# Revit family: equip-sink-elkay-double-lustertone-3322
name_source: partatom
category: Generic Models
units: mm (PartAtom-declared; Revit-internal decimal feet)

## family parameters
Always vertical = Yes
Can host rebar = No
Cut with Voids When Loaded = No
Part Type = Normal
Room Calculation Point = No
Round Connector Dimension = Use Diameter
Shared = No
Work Plane-Based = No

## types (1)
- ByType
    2D Hole 1 = No
    2D Hole 2 = No
    2D Hole 3 = No
    2D Hole 4 = No
    2D Hole 5 = No
    Bowl Length = 1' - 1 1/2"
    CL Sink to CL Partition = 0' - 0"
    Custom Bowl = No
    Custom Bowl Length = 1' - 1 1/2"
    Description = Lustertone Double Bowl Sink
    Drain Location = 0' - 7"
    Faucet Hole CL = 0' - 1 3/4"
    Hole 1 Top = 0' - 2 23/128"
    Hole 1 from CL = 0' - 4"
    Hole 1 to 2 = 0' - 4"
    Hole 1 to 3 = 0' - 8"
    Hole 1 to 4 = 1' - 0"
    Hole 1 to 5 = 1' - 3"
    Hole 2 Top = 0' - 2 23/128"
    Hole 3 Top = 0' - 2 23/128"
    Hole 4 Top = 0' - 2 23/128"
    Hole 5 Top = 0' - 1 1/2"
    Installation Sheet URL = http://www.elkayusa.com
    Left Bowl Length = 1' - 1 1/2"
    Manufacturer = Elkay Manufacturing
    Model = LR3322
    Partition Width = 0' - 1 1/4"
    Sink Bowl Formula = 1' - 1 1/2"
    Sink Depth = 0' - 7 5/8"
    Sink Ledge Back Width = 0' - 4 1/8"
    Sink Ledge Front Width = 0' - 1 7/8"
    Sink Ledge Sides Width = 0' - 2 3/8"
    Sink Length = 2' - 9"
    Sink Material = Metal - Steel - Stainless - Chrome
    Sink Width = 1' - 7 1/2"
    Specification Sheet URL = http://www.elkayusa.com
    URL = www.elkayusa.com

## geometry (parser evidence)
native form markers: Sweep x7
no freeform markers — native parametric forms only
